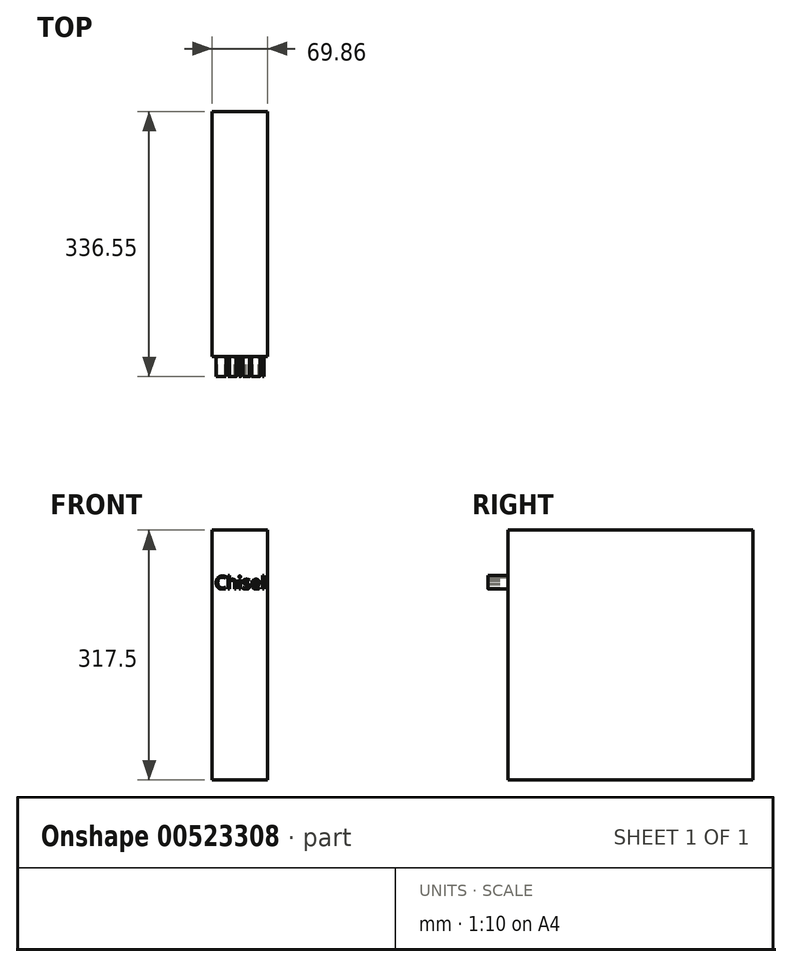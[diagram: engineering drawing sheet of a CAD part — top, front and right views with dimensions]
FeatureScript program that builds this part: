
annotation { "Feature Type Name" : "Feature", "Feature Type Description" : "" }
export const myFeature = defineFeature(function(context is Context, id is Id, definition is map)
    precondition{}
    {
        {
            var Q0;
            Q0=qCreatedBy(makeId("Front.planeOp"),FACE);
            var sketch = newSketch(context, id + "F0", { "sketchPlane" : qUnion([Q0])});
            skLineSegment(sketch, "E0.bottom", {"start": v(34.92, 158.75) * mm, "end": v(-34.93, 158.75) * mm});
            skLineSegment(sketch, "E0.top", {"start": v(34.92, -158.75) * mm, "end": v(-34.93, -158.75) * mm});
            skLineSegment(sketch, "E0.left", {"start": v(34.92, 158.75) * mm, "end": v(34.92, -158.75) * mm});
            skLineSegment(sketch, "E0.right", {"start": v(-34.93, 158.75) * mm, "end": v(-34.93, -158.75) * mm});
            skPoint(sketch, "E0.middle", {"position": v(0, 0) * mm});
            skSolve(sketch);
        }
        {
            var Q0;
            Q0=makeQuery(id+"F0.imprint","IMPRINT",FACE,{"disambiguationData":[TD([[makeQuery(id+"F0.imprint","IMPRINT",EDGE,{"derivedFrom":sQuery(id+"F0.wireOp",EDGE,"E0.bottom")}),1.0]])]});
            extrude(context, id + "F1", {"entities" : qUnion([Q0]), "depth" : 311.15 * mm, "offsetDistance" : 25.4 * mm});
        }
        {
            var Q0;
            Q0=makeQuery(id+"F1.opExtrude","CAP_FACE",FACE,{"disambiguationData":[OSD([sQuery(id+"F0.wireOp",EDGE,"E0.bottom"),sQuery(id+"F0.wireOp",EDGE,"E0.top"),sQuery(id+"F0.wireOp",EDGE,"E0.left"),sQuery(id+"F0.wireOp",EDGE,"E0.right")])],"isStart":false});
            var sketch = newSketch(context, id + "F2", { "sketchPlane" : qUnion([Q0])});
            skText(sketch, "E1", { "text": "Chisel", "fontName": "OpenSans-Regular.ttf"});
            const initialGuessF2  = {"E1": [-0.03143, 0.08383, 1, 0, 0.01652]};
            skSetInitialGuess(sketch, initialGuessF2);
            skSolve(sketch);
        }
        {
            var Q0;
            Q0 = qSketchRegion(id + "F2", true);
            extrude(context, id + "F3", {"entities" : qUnion([Q0]), "operationType" : NewBodyOperationType.ADD, "depth" : 25.4 * mm, "offsetDistance" : 25.4 * mm});
        }
    });
